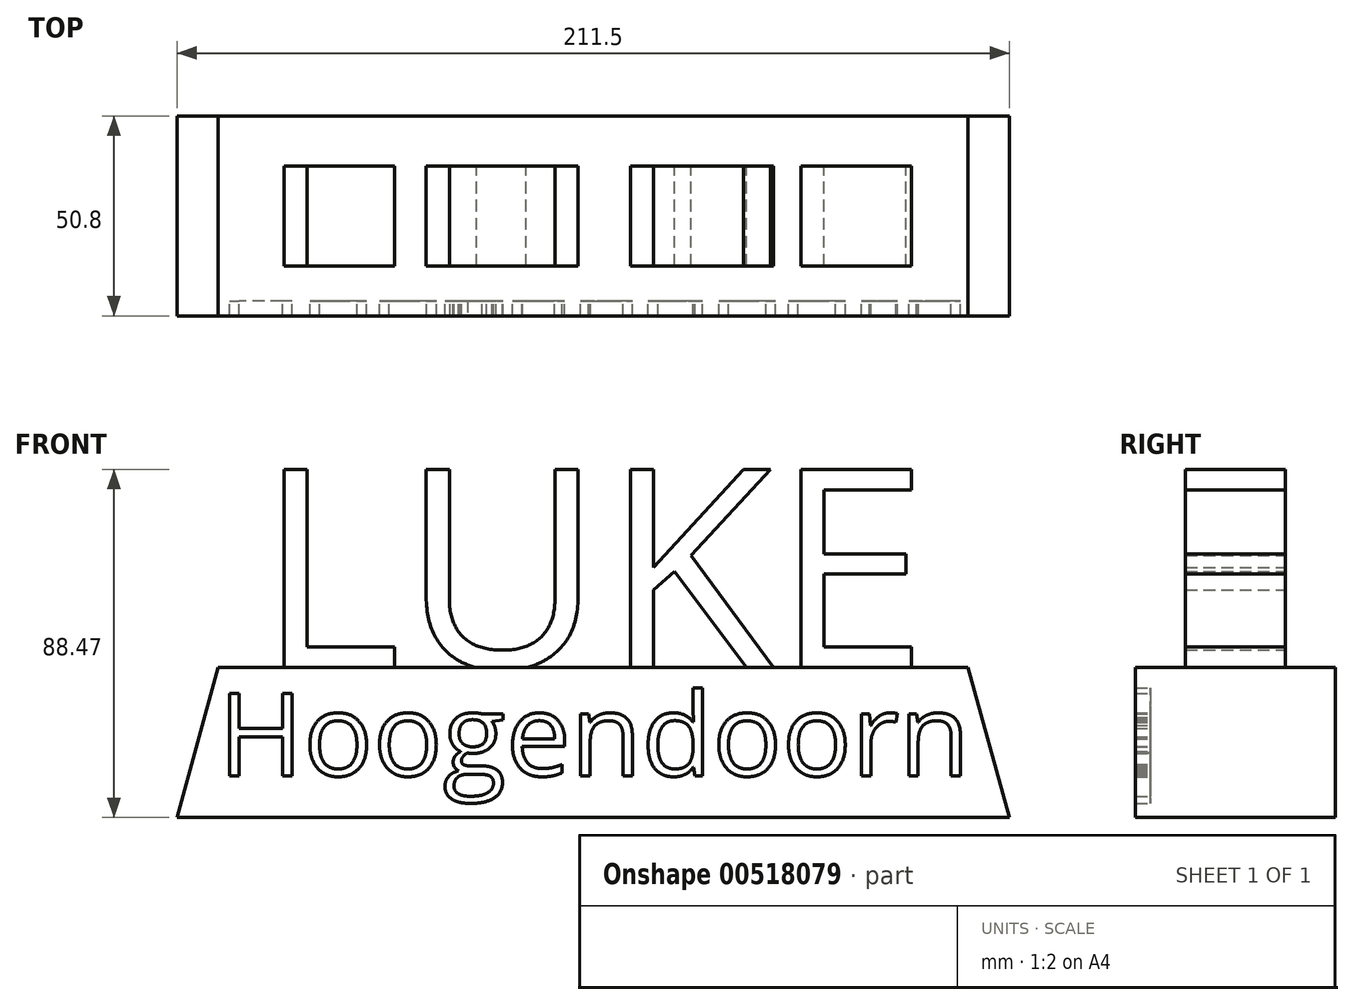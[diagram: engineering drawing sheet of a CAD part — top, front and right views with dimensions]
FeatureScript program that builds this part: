
annotation { "Feature Type Name" : "Feature", "Feature Type Description" : "" }
export const myFeature = defineFeature(function(context is Context, id is Id, definition is map)
    precondition{}
    {
        {
            var Q0;
            Q0=qCreatedBy(makeId("Front.planeOp"),FACE);
            var sketch = newSketch(context, id + "F0", { "sketchPlane" : qUnion([Q0])});
            skText(sketch, "E0", { "text": "LUKE\n", "fontName": "OpenSans-Regular.ttf"});
            skLineSegment(sketch, "E1.bottom", {"start": v(95.25, 0) * mm, "end": v(-95.25, 0) * mm});
            skLineSegment(sketch, "E1.top", {"start": v(95.25, -38.1) * mm, "end": v(-95.25, -38.1) * mm});
            skLineSegment(sketch, "E1.left", {"start": v(95.25, -6.35) * mm, "end": v(95.25, -27.46) * mm});
            skLineSegment(sketch, "E1.right", {"start": v(-95.25, -6.35) * mm, "end": v(-95.25, -27.46) * mm});
            skPoint(sketch, "E1.middle", {"position": v(0, -19.05) * mm});
            skLineSegment(sketch, "E2", {"start": v(-95.25, -6.35) * mm, "end": v(95.25, -6.35) * mm});
            skLineSegment(sketch, "E3.MirrorCS", {"start": v(-95.25, -27.46) * mm, "end": v(95.25, -27.46) * mm});
            skPoint(sketch, "E4.orphan", {"position": v(-95.25, -19.05) * mm});
            skPoint(sketch, "E5.end.orphan", {"position": v(95.25, -19.05) * mm});
            skText(sketch, "E6", { "text": "Hoogendoorn\n", "fontName": "OpenSans-Regular.ttf"});
            skLineSegment(sketch, "E7", {"start": v(-95.25, 0) * mm, "end": v(-105.75, -38.1) * mm});
            skLineSegment(sketch, "E8", {"start": v(-105.75, -38.1) * mm, "end": v(-95.25, -38.1) * mm});
            skLineSegment(sketch, "E9.MirrorCS", {"start": v(105.75, -38.1) * mm, "end": v(95.25, -38.1) * mm});
            skLineSegment(sketch, "E10.MirrorCS", {"start": v(95.25, 0) * mm, "end": v(105.75, -38.1) * mm});
            const initialGuessF0  = {"E0": [-0.08543, 0, 1, 0, 0.0508], "E6": [-0.09525, -0.02746, 1, 0, 0.02111]};
            skSetInitialGuess(sketch, initialGuessF0);
            skSolve(sketch);
        }
        {
            var Q0;
            Q0 = qSketchRegion(id + "F0", true);
            var Q1;
            Q1=makeQuery(id+"F0.imprint","IMPRINT",FACE,{"disambiguationData":[TD([[makeQuery(id+"F0.imprint","IMPRINT",EDGE,{"derivedFrom":sQuery(id+"F0.wireOp",EDGE,"E6.sketch_text.stroke-0")}),-1.0]])]});
            var Q2;
            {var subQ0=sQuery(id+"F0.wireOp",EDGE,"E6.sketch_text.stroke-1");Q2=makeQuery(id+"F0.imprint","IMPRINT",FACE,{"disambiguationData":[TD([[makeQuery(id+"F0.imprint","IMPRINT",EDGE,{"derivedFrom":subQ0}),1.0]])]});}
            var Q3;
            {var subQ29=sQuery(id+"F0.wireOp",EDGE,"E1.right");Q3=makeQuery(id+"F0.imprint","IMPRINT",FACE,{"disambiguationData":[TD([[makeQuery(id+"F0.imprint","IMPRINT",EDGE,{"derivedFrom":subQ29}),1.0]])]});}
            var Q4;
            {var subQ6=sQuery(id+"F0.wireOp",EDGE,"E6.sketch_text.stroke-29");Q4=makeQuery(id+"F0.imprint","IMPRINT",FACE,{"disambiguationData":[TD([[makeQuery(id+"F0.imprint","IMPRINT",EDGE,{"derivedFrom":subQ6}),-1.0]])]});}
            var Q5;
            {var subQ0=sQuery(id+"F0.wireOp",EDGE,"E6.sketch_text.stroke-31");var subQ1=sQuery(id+"F0.wireOp",EDGE,"E3.MirrorCS");var subQ2=makeQuery(id+"F0.imprint","INTERSECT",VERTEX,{"derivedFrom":[subQ1,subQ0]});Q5=makeQuery(id+"F0.imprint","IMPRINT",FACE,{"disambiguationData":[TD([[makeQuery(id+"F0.imprint","IMPRINT",EDGE,{"disambiguationData":[TD([[subQ2,-1.0]])],"derivedFrom":subQ1}),-1.0]])]});}
            var Q6;
            Q6=makeQuery(id+"F0.imprint","IMPRINT",FACE,{"disambiguationData":[TD([[makeQuery(id+"F0.imprint","IMPRINT",EDGE,{"derivedFrom":sQuery(id+"F0.wireOp",EDGE,"E6.sketch_text.stroke-38")}),1.0]])]});
            var Q7;
            Q7=makeQuery(id+"F0.imprint","IMPRINT",FACE,{"disambiguationData":[TD([[makeQuery(id+"F0.imprint","IMPRINT",EDGE,{"derivedFrom":sQuery(id+"F0.wireOp",EDGE,"E6.sketch_text.stroke-21")}),1.0]])]});
            var Q8;
            {var subQ6=sQuery(id+"F0.wireOp",EDGE,"E6.sketch_text.stroke-12");Q8=makeQuery(id+"F0.imprint","IMPRINT",FACE,{"disambiguationData":[TD([[makeQuery(id+"F0.imprint","IMPRINT",EDGE,{"derivedFrom":subQ6}),-1.0]])]});}
            var Q9;
            {var subQ0=sQuery(id+"F0.wireOp",EDGE,"E6.sketch_text.stroke-14");var subQ1=sQuery(id+"F0.wireOp",EDGE,"E3.MirrorCS");var subQ2=makeQuery(id+"F0.imprint","INTERSECT",VERTEX,{"derivedFrom":[subQ1,subQ0]});Q9=makeQuery(id+"F0.imprint","IMPRINT",FACE,{"disambiguationData":[TD([[makeQuery(id+"F0.imprint","IMPRINT",EDGE,{"disambiguationData":[TD([[subQ2,-1.0]])],"derivedFrom":subQ1}),-1.0]])]});}
            var Q10;
            Q10=makeQuery(id+"F0.imprint","IMPRINT",FACE,{"disambiguationData":[TD([[makeQuery(id+"F0.imprint","IMPRINT",EDGE,{"derivedFrom":sQuery(id+"F0.wireOp",EDGE,"E6.sketch_text.stroke-84")}),1.0]])]});
            var Q11;
            Q11=makeQuery(id+"F0.imprint","IMPRINT",FACE,{"disambiguationData":[TD([[makeQuery(id+"F0.imprint","IMPRINT",EDGE,{"derivedFrom":sQuery(id+"F0.wireOp",EDGE,"E6.sketch_text.stroke-46")}),-1.0]])]});
            var Q12;
            {var subQ5=sQuery(id+"F0.wireOp",EDGE,"E6.sketch_text.stroke-81");Q12=makeQuery(id+"F0.imprint","IMPRINT",FACE,{"disambiguationData":[TD([[makeQuery(id+"F0.imprint","IMPRINT",EDGE,{"derivedFrom":subQ5}),1.0]])]});}
            var Q13;
            Q13=makeQuery(id+"F0.imprint","IMPRINT",FACE,{"disambiguationData":[TD([[makeQuery(id+"F0.imprint","IMPRINT",EDGE,{"derivedFrom":sQuery(id+"F0.wireOp",EDGE,"E6.sketch_text.stroke-75")}),1.0]])]});
            var Q14;
            {var subQ11=sQuery(id+"F0.wireOp",EDGE,"E6.sketch_text.stroke-59");Q14=makeQuery(id+"F0.imprint","IMPRINT",FACE,{"disambiguationData":[TD([[makeQuery(id+"F0.imprint","IMPRINT",EDGE,{"derivedFrom":subQ11}),-1.0]])]});}
            var Q15;
            Q15=makeQuery(id+"F0.imprint","IMPRINT",FACE,{"disambiguationData":[TD([[makeQuery(id+"F0.imprint","IMPRINT",EDGE,{"derivedFrom":sQuery(id+"F0.wireOp",EDGE,"E6.sketch_text.stroke-104")}),1.0]])]});
            var Q16;
            {var subQ5=sQuery(id+"F0.wireOp",EDGE,"E6.sketch_text.stroke-91");Q16=makeQuery(id+"F0.imprint","IMPRINT",FACE,{"disambiguationData":[TD([[makeQuery(id+"F0.imprint","IMPRINT",EDGE,{"derivedFrom":subQ5}),-1.0]])]});}
            var Q17;
            {var subQ5=sQuery(id+"F0.wireOp",EDGE,"E6.sketch_text.stroke-103");Q17=makeQuery(id+"F0.imprint","IMPRINT",FACE,{"disambiguationData":[TD([[makeQuery(id+"F0.imprint","IMPRINT",EDGE,{"derivedFrom":subQ5}),-1.0]])]});}
            var Q18;
            {var subQ0=sQuery(id+"F0.wireOp",EDGE,"E6.sketch_text.stroke-109");Q18=makeQuery(id+"F0.imprint","IMPRINT",FACE,{"disambiguationData":[TD([[makeQuery(id+"F0.imprint","IMPRINT",EDGE,{"derivedFrom":subQ0}),1.0]])]});}
            var Q19;
            Q19=makeQuery(id+"F0.imprint","IMPRINT",FACE,{"disambiguationData":[TD([[makeQuery(id+"F0.imprint","IMPRINT",EDGE,{"derivedFrom":sQuery(id+"F0.wireOp",EDGE,"E6.sketch_text.stroke-109")}),-1.0]])]});
            var Q20;
            {var subQ9=sQuery(id+"F0.wireOp",EDGE,"E6.sketch_text.stroke-126");Q20=makeQuery(id+"F0.imprint","IMPRINT",FACE,{"disambiguationData":[TD([[makeQuery(id+"F0.imprint","IMPRINT",EDGE,{"derivedFrom":subQ9}),-1.0]])]});}
            var Q21;
            Q21=makeQuery(id+"F0.imprint","IMPRINT",FACE,{"disambiguationData":[TD([[makeQuery(id+"F0.imprint","IMPRINT",EDGE,{"derivedFrom":sQuery(id+"F0.wireOp",EDGE,"E6.sketch_text.stroke-141")}),1.0]])]});
            var Q22;
            {var subQ4=sQuery(id+"F0.wireOp",EDGE,"E6.sketch_text.stroke-126");Q22=makeQuery(id+"F0.imprint","IMPRINT",FACE,{"disambiguationData":[TD([[makeQuery(id+"F0.imprint","IMPRINT",EDGE,{"derivedFrom":subQ4}),1.0]])]});}
            var Q23;
            {var subQ5=sQuery(id+"F0.wireOp",EDGE,"E6.sketch_text.stroke-137");Q23=makeQuery(id+"F0.imprint","IMPRINT",FACE,{"disambiguationData":[TD([[makeQuery(id+"F0.imprint","IMPRINT",EDGE,{"derivedFrom":subQ5}),-1.0]])]});}
            var Q24;
            {var subQ0=sQuery(id+"F0.wireOp",EDGE,"E6.sketch_text.stroke-128");var subQ1=sQuery(id+"F0.wireOp",EDGE,"E3.MirrorCS");var subQ2=makeQuery(id+"F0.imprint","INTERSECT",VERTEX,{"derivedFrom":[subQ1,subQ0]});Q24=makeQuery(id+"F0.imprint","IMPRINT",FACE,{"disambiguationData":[TD([[makeQuery(id+"F0.imprint","IMPRINT",EDGE,{"disambiguationData":[TD([[subQ2,-1.0]])],"derivedFrom":subQ1}),-1.0]])]});}
            var Q25;
            Q25=makeQuery(id+"F0.imprint","IMPRINT",FACE,{"disambiguationData":[TD([[makeQuery(id+"F0.imprint","IMPRINT",EDGE,{"derivedFrom":sQuery(id+"F0.wireOp",EDGE,"E6.sketch_text.stroke-159")}),1.0]])]});
            var Q26;
            {var subQ6=sQuery(id+"F0.wireOp",EDGE,"E6.sketch_text.stroke-150");Q26=makeQuery(id+"F0.imprint","IMPRINT",FACE,{"disambiguationData":[TD([[makeQuery(id+"F0.imprint","IMPRINT",EDGE,{"derivedFrom":subQ6}),-1.0]])]});}
            var Q27;
            {var subQ3=sQuery(id+"F0.wireOp",EDGE,"E1.left");Q27=makeQuery(id+"F0.imprint","IMPRINT",FACE,{"disambiguationData":[TD([[makeQuery(id+"F0.imprint","IMPRINT",EDGE,{"derivedFrom":subQ3}),-1.0]])]});}
            var Q28;
            Q28=makeQuery(id+"F0.imprint","IMPRINT",FACE,{"disambiguationData":[TD([[makeQuery(id+"F0.imprint","IMPRINT",EDGE,{"derivedFrom":sQuery(id+"F0.wireOp",EDGE,"E6.sketch_text.stroke-176")}),1.0]])]});
            var Q29;
            {var subQ6=sQuery(id+"F0.wireOp",EDGE,"E6.sketch_text.stroke-167");Q29=makeQuery(id+"F0.imprint","IMPRINT",FACE,{"disambiguationData":[TD([[makeQuery(id+"F0.imprint","IMPRINT",EDGE,{"derivedFrom":subQ6}),-1.0]])]});}
            var Q30;
            {var subQ0=sQuery(id+"F0.wireOp",EDGE,"E6.sketch_text.stroke-169");var subQ1=sQuery(id+"F0.wireOp",EDGE,"E3.MirrorCS");var subQ2=makeQuery(id+"F0.imprint","INTERSECT",VERTEX,{"derivedFrom":[subQ1,subQ0]});Q30=makeQuery(id+"F0.imprint","IMPRINT",FACE,{"disambiguationData":[TD([[makeQuery(id+"F0.imprint","IMPRINT",EDGE,{"disambiguationData":[TD([[subQ2,-1.0]])],"derivedFrom":subQ1}),-1.0]])]});}
            var Q31;
            {var subQ0=sQuery(id+"F0.wireOp",EDGE,"E6.sketch_text.stroke-152");var subQ1=sQuery(id+"F0.wireOp",EDGE,"E3.MirrorCS");var subQ2=makeQuery(id+"F0.imprint","INTERSECT",VERTEX,{"derivedFrom":[subQ1,subQ0]});Q31=makeQuery(id+"F0.imprint","IMPRINT",FACE,{"disambiguationData":[TD([[makeQuery(id+"F0.imprint","IMPRINT",EDGE,{"disambiguationData":[TD([[subQ2,-1.0]])],"derivedFrom":subQ1}),-1.0]])]});}
            var Q32;
            Q32=makeQuery(id+"F0.imprint","IMPRINT",FACE,{"disambiguationData":[TD([[makeQuery(id+"F0.imprint","IMPRINT",EDGE,{"derivedFrom":sQuery(id+"F0.wireOp",EDGE,"E6.sketch_text.stroke-184")}),-1.0]])]});
            var Q33;
            {var subQ0=sQuery(id+"F0.wireOp",EDGE,"E6.sketch_text.stroke-197");Q33=makeQuery(id+"F0.imprint","IMPRINT",FACE,{"disambiguationData":[TD([[makeQuery(id+"F0.imprint","IMPRINT",EDGE,{"derivedFrom":subQ0}),1.0]])]});}
            var Q34;
            Q34=makeQuery(id+"F0.imprint","IMPRINT",FACE,{"disambiguationData":[TD([[makeQuery(id+"F0.imprint","IMPRINT",EDGE,{"derivedFrom":sQuery(id+"F0.wireOp",EDGE,"E6.sketch_text.stroke-197")}),-1.0]])]});
            extrude(context, id + "F1", {"entities" : qUnion([Q0, Q1, Q2, Q3, Q4, Q5, Q6, Q7, Q8, Q9, Q10, Q11, Q12, Q13, Q14, Q15, Q16, Q17, Q18, Q19, Q20, Q21, Q22, Q23, Q24, Q25, Q26, Q27, Q28, Q29, Q30, Q31, Q32, Q33, Q34]), "depth" : 25.4 * mm, "offsetDistance" : 25.4 * mm});
        }
        {
            var Q0;
            {var subQ6=sQuery(id+"F0.wireOp",EDGE,"E6.sketch_text.stroke-12");Q0=makeQuery(id+"F0.imprint","IMPRINT",FACE,{"disambiguationData":[TD([[makeQuery(id+"F0.imprint","IMPRINT",EDGE,{"derivedFrom":subQ6}),-1.0]])]});}
            var Q1;
            Q1=makeQuery(id+"F0.imprint","IMPRINT",FACE,{"disambiguationData":[TD([[makeQuery(id+"F0.imprint","IMPRINT",EDGE,{"derivedFrom":sQuery(id+"F0.wireOp",EDGE,"E6.sketch_text.stroke-0")}),-1.0]])]});
            var Q2;
            {var subQ0=sQuery(id+"F0.wireOp",EDGE,"E6.sketch_text.stroke-14");var subQ1=sQuery(id+"F0.wireOp",EDGE,"E3.MirrorCS");var subQ2=makeQuery(id+"F0.imprint","INTERSECT",VERTEX,{"derivedFrom":[subQ1,subQ0]});Q2=makeQuery(id+"F0.imprint","IMPRINT",FACE,{"disambiguationData":[TD([[makeQuery(id+"F0.imprint","IMPRINT",EDGE,{"disambiguationData":[TD([[subQ2,-1.0]])],"derivedFrom":subQ1}),-1.0]])]});}
            var Q3;
            {var subQ6=sQuery(id+"F0.wireOp",EDGE,"E6.sketch_text.stroke-29");Q3=makeQuery(id+"F0.imprint","IMPRINT",FACE,{"disambiguationData":[TD([[makeQuery(id+"F0.imprint","IMPRINT",EDGE,{"derivedFrom":subQ6}),-1.0]])]});}
            var Q4;
            {var subQ0=sQuery(id+"F0.wireOp",EDGE,"E6.sketch_text.stroke-31");var subQ1=sQuery(id+"F0.wireOp",EDGE,"E3.MirrorCS");var subQ2=makeQuery(id+"F0.imprint","INTERSECT",VERTEX,{"derivedFrom":[subQ1,subQ0]});Q4=makeQuery(id+"F0.imprint","IMPRINT",FACE,{"disambiguationData":[TD([[makeQuery(id+"F0.imprint","IMPRINT",EDGE,{"disambiguationData":[TD([[subQ2,-1.0]])],"derivedFrom":subQ1}),-1.0]])]});}
            var Q5;
            {var subQ11=sQuery(id+"F0.wireOp",EDGE,"E6.sketch_text.stroke-59");Q5=makeQuery(id+"F0.imprint","IMPRINT",FACE,{"disambiguationData":[TD([[makeQuery(id+"F0.imprint","IMPRINT",EDGE,{"derivedFrom":subQ11}),-1.0]])]});}
            var Q6;
            Q6=makeQuery(id+"F0.imprint","IMPRINT",FACE,{"disambiguationData":[TD([[makeQuery(id+"F0.imprint","IMPRINT",EDGE,{"derivedFrom":sQuery(id+"F0.wireOp",EDGE,"E6.sketch_text.stroke-46")}),-1.0]])]});
            var Q7;
            {var subQ5=sQuery(id+"F0.wireOp",EDGE,"E6.sketch_text.stroke-91");Q7=makeQuery(id+"F0.imprint","IMPRINT",FACE,{"disambiguationData":[TD([[makeQuery(id+"F0.imprint","IMPRINT",EDGE,{"derivedFrom":subQ5}),-1.0]])]});}
            var Q8;
            Q8=makeQuery(id+"F0.imprint","IMPRINT",FACE,{"disambiguationData":[TD([[makeQuery(id+"F0.imprint","IMPRINT",EDGE,{"derivedFrom":sQuery(id+"F0.wireOp",EDGE,"E6.sketch_text.stroke-109")}),-1.0]])]});
            var Q9;
            {var subQ9=sQuery(id+"F0.wireOp",EDGE,"E6.sketch_text.stroke-126");Q9=makeQuery(id+"F0.imprint","IMPRINT",FACE,{"disambiguationData":[TD([[makeQuery(id+"F0.imprint","IMPRINT",EDGE,{"derivedFrom":subQ9}),-1.0]])]});}
            var Q10;
            {var subQ5=sQuery(id+"F0.wireOp",EDGE,"E6.sketch_text.stroke-137");Q10=makeQuery(id+"F0.imprint","IMPRINT",FACE,{"disambiguationData":[TD([[makeQuery(id+"F0.imprint","IMPRINT",EDGE,{"derivedFrom":subQ5}),-1.0]])]});}
            var Q11;
            {var subQ0=sQuery(id+"F0.wireOp",EDGE,"E6.sketch_text.stroke-128");var subQ1=sQuery(id+"F0.wireOp",EDGE,"E3.MirrorCS");var subQ2=makeQuery(id+"F0.imprint","INTERSECT",VERTEX,{"derivedFrom":[subQ1,subQ0]});Q11=makeQuery(id+"F0.imprint","IMPRINT",FACE,{"disambiguationData":[TD([[makeQuery(id+"F0.imprint","IMPRINT",EDGE,{"disambiguationData":[TD([[subQ2,-1.0]])],"derivedFrom":subQ1}),-1.0]])]});}
            var Q12;
            {var subQ5=sQuery(id+"F0.wireOp",EDGE,"E6.sketch_text.stroke-103");Q12=makeQuery(id+"F0.imprint","IMPRINT",FACE,{"disambiguationData":[TD([[makeQuery(id+"F0.imprint","IMPRINT",EDGE,{"derivedFrom":subQ5}),-1.0]])]});}
            var Q13;
            {var subQ6=sQuery(id+"F0.wireOp",EDGE,"E6.sketch_text.stroke-150");Q13=makeQuery(id+"F0.imprint","IMPRINT",FACE,{"disambiguationData":[TD([[makeQuery(id+"F0.imprint","IMPRINT",EDGE,{"derivedFrom":subQ6}),-1.0]])]});}
            var Q14;
            {var subQ0=sQuery(id+"F0.wireOp",EDGE,"E6.sketch_text.stroke-152");var subQ1=sQuery(id+"F0.wireOp",EDGE,"E3.MirrorCS");var subQ2=makeQuery(id+"F0.imprint","INTERSECT",VERTEX,{"derivedFrom":[subQ1,subQ0]});Q14=makeQuery(id+"F0.imprint","IMPRINT",FACE,{"disambiguationData":[TD([[makeQuery(id+"F0.imprint","IMPRINT",EDGE,{"disambiguationData":[TD([[subQ2,-1.0]])],"derivedFrom":subQ1}),-1.0]])]});}
            var Q15;
            {var subQ6=sQuery(id+"F0.wireOp",EDGE,"E6.sketch_text.stroke-167");Q15=makeQuery(id+"F0.imprint","IMPRINT",FACE,{"disambiguationData":[TD([[makeQuery(id+"F0.imprint","IMPRINT",EDGE,{"derivedFrom":subQ6}),-1.0]])]});}
            var Q16;
            {var subQ0=sQuery(id+"F0.wireOp",EDGE,"E6.sketch_text.stroke-169");var subQ1=sQuery(id+"F0.wireOp",EDGE,"E3.MirrorCS");var subQ2=makeQuery(id+"F0.imprint","INTERSECT",VERTEX,{"derivedFrom":[subQ1,subQ0]});Q16=makeQuery(id+"F0.imprint","IMPRINT",FACE,{"disambiguationData":[TD([[makeQuery(id+"F0.imprint","IMPRINT",EDGE,{"disambiguationData":[TD([[subQ2,-1.0]])],"derivedFrom":subQ1}),-1.0]])]});}
            var Q17;
            Q17=makeQuery(id+"F0.imprint","IMPRINT",FACE,{"disambiguationData":[TD([[makeQuery(id+"F0.imprint","IMPRINT",EDGE,{"derivedFrom":sQuery(id+"F0.wireOp",EDGE,"E6.sketch_text.stroke-184")}),-1.0]])]});
            var Q18;
            Q18=makeQuery(id+"F0.imprint","IMPRINT",FACE,{"disambiguationData":[TD([[makeQuery(id+"F0.imprint","IMPRINT",EDGE,{"derivedFrom":sQuery(id+"F0.wireOp",EDGE,"E6.sketch_text.stroke-197")}),-1.0]])]});
            extrude(context, id + "F2", {"entities" : qUnion([Q0, Q1, Q2, Q3, Q4, Q5, Q6, Q7, Q8, Q9, Q10, Q11, Q12, Q13, Q14, Q15, Q16, Q17, Q18]), "operationType" : NewBodyOperationType.REMOVE, "depth" : 25.4 * mm, "offsetDistance" : 25.4 * mm, "hasSecondDirection" : true, "secondDirectionOppositeDirection" : false, "secondDirectionDepth" : 21.59 * mm});
        }
        {
            var Q0;
            {var subQ0=sQuery(id+"F0.wireOp",EDGE,"E10.MirrorCS");var subQ1=sQuery(id+"F0.wireOp",EDGE,"E7");var subQ2=sQuery(id+"F0.wireOp",EDGE,"E9.MirrorCS");var subQ3=sQuery(id+"F0.wireOp",EDGE,"E8");var subQ4=sQuery(id+"F0.wireOp",EDGE,"E1.top");var subQ5=sQuery(id+"F0.wireOp",EDGE,"E1.bottom");var subQ6=sQuery(id+"F0.wireOp",EDGE,"E0.sketch_text.stroke-0");var subQ7=sQuery(id+"F0.wireOp",EDGE,"E0.sketch_text.stroke-21");var subQ8=sQuery(id+"F0.wireOp",EDGE,"E0.sketch_text.stroke-23");var subQ9=sQuery(id+"F0.wireOp",EDGE,"E0.sketch_text.stroke-36");var subQ10=sQuery(id+"F0.wireOp",EDGE,"E0.sketch_text.stroke-35");var subQ11=sQuery(id+"F0.wireOp",EDGE,"E0.sketch_text.stroke-34");var subQ12=sQuery(id+"F0.wireOp",EDGE,"E0.sketch_text.stroke-33");var subQ13=sQuery(id+"F0.wireOp",EDGE,"E0.sketch_text.stroke-31");var subQ14=sQuery(id+"F0.wireOp",EDGE,"E0.sketch_text.stroke-30");var subQ15=sQuery(id+"F0.wireOp",EDGE,"E0.sketch_text.stroke-29");var subQ16=sQuery(id+"F0.wireOp",EDGE,"E0.sketch_text.stroke-28");var subQ17=sQuery(id+"F0.wireOp",EDGE,"E0.sketch_text.stroke-27");var subQ18=sQuery(id+"F0.wireOp",EDGE,"E0.sketch_text.stroke-26");var subQ19=sQuery(id+"F0.wireOp",EDGE,"E0.sketch_text.stroke-25");var subQ20=sQuery(id+"F0.wireOp",EDGE,"E0.sketch_text.stroke-22");var subQ21=sQuery(id+"F0.wireOp",EDGE,"E0.sketch_text.stroke-17");var subQ22=sQuery(id+"F0.wireOp",EDGE,"E0.sketch_text.stroke-16");var subQ23=sQuery(id+"F0.wireOp",EDGE,"E0.sketch_text.stroke-15");var subQ24=sQuery(id+"F0.wireOp",EDGE,"E0.sketch_text.stroke-14");var subQ25=sQuery(id+"F0.wireOp",EDGE,"E0.sketch_text.stroke-13");var subQ26=sQuery(id+"F0.wireOp",EDGE,"E0.sketch_text.stroke-12");var subQ27=sQuery(id+"F0.wireOp",EDGE,"E0.sketch_text.stroke-11");var subQ28=sQuery(id+"F0.wireOp",EDGE,"E0.sketch_text.stroke-10");var subQ29=sQuery(id+"F0.wireOp",EDGE,"E0.sketch_text.stroke-9");var subQ30=sQuery(id+"F0.wireOp",EDGE,"E0.sketch_text.stroke-8");var subQ31=sQuery(id+"F0.wireOp",EDGE,"E0.sketch_text.stroke-7");var subQ32=sQuery(id+"F0.wireOp",EDGE,"E0.sketch_text.stroke-6");var subQ33=sQuery(id+"F0.wireOp",EDGE,"E0.sketch_text.stroke-4");var subQ34=sQuery(id+"F0.wireOp",EDGE,"E0.sketch_text.stroke-3");var subQ35=sQuery(id+"F0.wireOp",EDGE,"E0.sketch_text.stroke-2");var subQ36=sQuery(id+"F0.wireOp",EDGE,"E0.sketch_text.stroke-1");var subQ37=sQuery(id+"F0.wireOp",EDGE,"E0.sketch_text.stroke-43");var subQ38=sQuery(id+"F0.wireOp",EDGE,"E0.sketch_text.stroke-42");var subQ39=sQuery(id+"F0.wireOp",EDGE,"E0.sketch_text.stroke-41");var subQ40=sQuery(id+"F0.wireOp",EDGE,"E0.sketch_text.stroke-40");var subQ41=sQuery(id+"F0.wireOp",EDGE,"E0.sketch_text.stroke-39");var subQ42=sQuery(id+"F0.wireOp",EDGE,"E0.sketch_text.stroke-38");var subQ43=sQuery(id+"F0.wireOp",EDGE,"E0.sketch_text.stroke-37");var subQ44=sQuery(id+"F0.wireOp",EDGE,"E0.sketch_text.stroke-18");var subQ45=sQuery(id+"F0.wireOp",EDGE,"E0.sketch_text.stroke-19");Q0=makeQuery(id+"F2.boolean.opBoolean","SPLIT",FACE,{"disambiguationData":[TD([makeQuery(id+"F1.opExtrude","SWEPT_FACE",FACE,{"disambiguationData":[OSD([subQ6])]})])],"derivedFrom":makeQuery(id+"F1.opExtrude","CAP_FACE",FACE,{"disambiguationData":[OSD([subQ6,subQ36,subQ35,subQ34,subQ33,subQ32,subQ31,subQ30,subQ29,subQ28,subQ27,subQ26,subQ25,subQ24,subQ23,subQ22,subQ21,subQ44,subQ45,subQ7,subQ20,subQ8,subQ19,subQ18,subQ17,subQ16,subQ15,subQ14,subQ13,subQ12,subQ11,subQ10,subQ9,subQ43,subQ42,subQ41,subQ40,subQ39,subQ38,subQ37,subQ5,subQ4,subQ1,subQ3,subQ2,subQ0])],"isStart":false})});}
            var Q1;
            Q1=makeQuery(id+"F2.boolean.opBoolean","SPLIT",FACE,{"disambiguationData":[TD([makeQuery(id+"F2.opExtrude","SWEPT_FACE",FACE,{"disambiguationData":[OSD([sQuery(id+"F0.wireOp",EDGE,"E6.sketch_text.stroke-21")])]})])],"derivedFrom":makeQuery(id+"F1.opExtrude","CAP_FACE",FACE,{"disambiguationData":[OSD([sQuery(id+"F0.wireOp",EDGE,"E0.sketch_text.stroke-0"),sQuery(id+"F0.wireOp",EDGE,"E0.sketch_text.stroke-1"),sQuery(id+"F0.wireOp",EDGE,"E0.sketch_text.stroke-2"),sQuery(id+"F0.wireOp",EDGE,"E0.sketch_text.stroke-3"),sQuery(id+"F0.wireOp",EDGE,"E0.sketch_text.stroke-4"),sQuery(id+"F0.wireOp",EDGE,"E0.sketch_text.stroke-6"),sQuery(id+"F0.wireOp",EDGE,"E0.sketch_text.stroke-7"),sQuery(id+"F0.wireOp",EDGE,"E0.sketch_text.stroke-8"),sQuery(id+"F0.wireOp",EDGE,"E0.sketch_text.stroke-9"),sQuery(id+"F0.wireOp",EDGE,"E0.sketch_text.stroke-10"),sQuery(id+"F0.wireOp",EDGE,"E0.sketch_text.stroke-11"),sQuery(id+"F0.wireOp",EDGE,"E0.sketch_text.stroke-12"),sQuery(id+"F0.wireOp",EDGE,"E0.sketch_text.stroke-13"),sQuery(id+"F0.wireOp",EDGE,"E0.sketch_text.stroke-14"),sQuery(id+"F0.wireOp",EDGE,"E0.sketch_text.stroke-15"),sQuery(id+"F0.wireOp",EDGE,"E0.sketch_text.stroke-16"),sQuery(id+"F0.wireOp",EDGE,"E0.sketch_text.stroke-17"),sQuery(id+"F0.wireOp",EDGE,"E0.sketch_text.stroke-18"),sQuery(id+"F0.wireOp",EDGE,"E0.sketch_text.stroke-19"),sQuery(id+"F0.wireOp",EDGE,"E0.sketch_text.stroke-21"),sQuery(id+"F0.wireOp",EDGE,"E0.sketch_text.stroke-22"),sQuery(id+"F0.wireOp",EDGE,"E0.sketch_text.stroke-23"),sQuery(id+"F0.wireOp",EDGE,"E0.sketch_text.stroke-25"),sQuery(id+"F0.wireOp",EDGE,"E0.sketch_text.stroke-26"),sQuery(id+"F0.wireOp",EDGE,"E0.sketch_text.stroke-27"),sQuery(id+"F0.wireOp",EDGE,"E0.sketch_text.stroke-28"),sQuery(id+"F0.wireOp",EDGE,"E0.sketch_text.stroke-29"),sQuery(id+"F0.wireOp",EDGE,"E0.sketch_text.stroke-30"),sQuery(id+"F0.wireOp",EDGE,"E0.sketch_text.stroke-31"),sQuery(id+"F0.wireOp",EDGE,"E0.sketch_text.stroke-33"),sQuery(id+"F0.wireOp",EDGE,"E0.sketch_text.stroke-34"),sQuery(id+"F0.wireOp",EDGE,"E0.sketch_text.stroke-35"),sQuery(id+"F0.wireOp",EDGE,"E0.sketch_text.stroke-36"),sQuery(id+"F0.wireOp",EDGE,"E0.sketch_text.stroke-37"),sQuery(id+"F0.wireOp",EDGE,"E0.sketch_text.stroke-38"),sQuery(id+"F0.wireOp",EDGE,"E0.sketch_text.stroke-39"),sQuery(id+"F0.wireOp",EDGE,"E0.sketch_text.stroke-40"),sQuery(id+"F0.wireOp",EDGE,"E0.sketch_text.stroke-41"),sQuery(id+"F0.wireOp",EDGE,"E0.sketch_text.stroke-42"),sQuery(id+"F0.wireOp",EDGE,"E0.sketch_text.stroke-43"),sQuery(id+"F0.wireOp",EDGE,"E1.bottom"),sQuery(id+"F0.wireOp",EDGE,"E1.top"),sQuery(id+"F0.wireOp",EDGE,"E7"),sQuery(id+"F0.wireOp",EDGE,"E8"),sQuery(id+"F0.wireOp",EDGE,"E9.MirrorCS"),sQuery(id+"F0.wireOp",EDGE,"E10.MirrorCS")])],"isStart":false})});
            var Q2;
            Q2=makeQuery(id+"F2.boolean.opBoolean","SPLIT",FACE,{"disambiguationData":[TD([makeQuery(id+"F2.opExtrude","SWEPT_FACE",FACE,{"disambiguationData":[OSD([sQuery(id+"F0.wireOp",EDGE,"E6.sketch_text.stroke-38")])]})])],"derivedFrom":makeQuery(id+"F1.opExtrude","CAP_FACE",FACE,{"disambiguationData":[OSD([sQuery(id+"F0.wireOp",EDGE,"E0.sketch_text.stroke-0"),sQuery(id+"F0.wireOp",EDGE,"E0.sketch_text.stroke-1"),sQuery(id+"F0.wireOp",EDGE,"E0.sketch_text.stroke-2"),sQuery(id+"F0.wireOp",EDGE,"E0.sketch_text.stroke-3"),sQuery(id+"F0.wireOp",EDGE,"E0.sketch_text.stroke-4"),sQuery(id+"F0.wireOp",EDGE,"E0.sketch_text.stroke-6"),sQuery(id+"F0.wireOp",EDGE,"E0.sketch_text.stroke-7"),sQuery(id+"F0.wireOp",EDGE,"E0.sketch_text.stroke-8"),sQuery(id+"F0.wireOp",EDGE,"E0.sketch_text.stroke-9"),sQuery(id+"F0.wireOp",EDGE,"E0.sketch_text.stroke-10"),sQuery(id+"F0.wireOp",EDGE,"E0.sketch_text.stroke-11"),sQuery(id+"F0.wireOp",EDGE,"E0.sketch_text.stroke-12"),sQuery(id+"F0.wireOp",EDGE,"E0.sketch_text.stroke-13"),sQuery(id+"F0.wireOp",EDGE,"E0.sketch_text.stroke-14"),sQuery(id+"F0.wireOp",EDGE,"E0.sketch_text.stroke-15"),sQuery(id+"F0.wireOp",EDGE,"E0.sketch_text.stroke-16"),sQuery(id+"F0.wireOp",EDGE,"E0.sketch_text.stroke-17"),sQuery(id+"F0.wireOp",EDGE,"E0.sketch_text.stroke-18"),sQuery(id+"F0.wireOp",EDGE,"E0.sketch_text.stroke-19"),sQuery(id+"F0.wireOp",EDGE,"E0.sketch_text.stroke-21"),sQuery(id+"F0.wireOp",EDGE,"E0.sketch_text.stroke-22"),sQuery(id+"F0.wireOp",EDGE,"E0.sketch_text.stroke-23"),sQuery(id+"F0.wireOp",EDGE,"E0.sketch_text.stroke-25"),sQuery(id+"F0.wireOp",EDGE,"E0.sketch_text.stroke-26"),sQuery(id+"F0.wireOp",EDGE,"E0.sketch_text.stroke-27"),sQuery(id+"F0.wireOp",EDGE,"E0.sketch_text.stroke-28"),sQuery(id+"F0.wireOp",EDGE,"E0.sketch_text.stroke-29"),sQuery(id+"F0.wireOp",EDGE,"E0.sketch_text.stroke-30"),sQuery(id+"F0.wireOp",EDGE,"E0.sketch_text.stroke-31"),sQuery(id+"F0.wireOp",EDGE,"E0.sketch_text.stroke-33"),sQuery(id+"F0.wireOp",EDGE,"E0.sketch_text.stroke-34"),sQuery(id+"F0.wireOp",EDGE,"E0.sketch_text.stroke-35"),sQuery(id+"F0.wireOp",EDGE,"E0.sketch_text.stroke-36"),sQuery(id+"F0.wireOp",EDGE,"E0.sketch_text.stroke-37"),sQuery(id+"F0.wireOp",EDGE,"E0.sketch_text.stroke-38"),sQuery(id+"F0.wireOp",EDGE,"E0.sketch_text.stroke-39"),sQuery(id+"F0.wireOp",EDGE,"E0.sketch_text.stroke-40"),sQuery(id+"F0.wireOp",EDGE,"E0.sketch_text.stroke-41"),sQuery(id+"F0.wireOp",EDGE,"E0.sketch_text.stroke-42"),sQuery(id+"F0.wireOp",EDGE,"E0.sketch_text.stroke-43"),sQuery(id+"F0.wireOp",EDGE,"E1.bottom"),sQuery(id+"F0.wireOp",EDGE,"E1.top"),sQuery(id+"F0.wireOp",EDGE,"E7"),sQuery(id+"F0.wireOp",EDGE,"E8"),sQuery(id+"F0.wireOp",EDGE,"E9.MirrorCS"),sQuery(id+"F0.wireOp",EDGE,"E10.MirrorCS")])],"isStart":false})});
            var Q3;
            Q3=makeQuery(id+"F2.boolean.opBoolean","SPLIT",FACE,{"disambiguationData":[TD([makeQuery(id+"F2.opExtrude","SWEPT_FACE",FACE,{"disambiguationData":[OSD([sQuery(id+"F0.wireOp",EDGE,"E6.sketch_text.stroke-84")])]})])],"derivedFrom":makeQuery(id+"F1.opExtrude","CAP_FACE",FACE,{"disambiguationData":[OSD([sQuery(id+"F0.wireOp",EDGE,"E0.sketch_text.stroke-0"),sQuery(id+"F0.wireOp",EDGE,"E0.sketch_text.stroke-1"),sQuery(id+"F0.wireOp",EDGE,"E0.sketch_text.stroke-2"),sQuery(id+"F0.wireOp",EDGE,"E0.sketch_text.stroke-3"),sQuery(id+"F0.wireOp",EDGE,"E0.sketch_text.stroke-4"),sQuery(id+"F0.wireOp",EDGE,"E0.sketch_text.stroke-6"),sQuery(id+"F0.wireOp",EDGE,"E0.sketch_text.stroke-7"),sQuery(id+"F0.wireOp",EDGE,"E0.sketch_text.stroke-8"),sQuery(id+"F0.wireOp",EDGE,"E0.sketch_text.stroke-9"),sQuery(id+"F0.wireOp",EDGE,"E0.sketch_text.stroke-10"),sQuery(id+"F0.wireOp",EDGE,"E0.sketch_text.stroke-11"),sQuery(id+"F0.wireOp",EDGE,"E0.sketch_text.stroke-12"),sQuery(id+"F0.wireOp",EDGE,"E0.sketch_text.stroke-13"),sQuery(id+"F0.wireOp",EDGE,"E0.sketch_text.stroke-14"),sQuery(id+"F0.wireOp",EDGE,"E0.sketch_text.stroke-15"),sQuery(id+"F0.wireOp",EDGE,"E0.sketch_text.stroke-16"),sQuery(id+"F0.wireOp",EDGE,"E0.sketch_text.stroke-17"),sQuery(id+"F0.wireOp",EDGE,"E0.sketch_text.stroke-18"),sQuery(id+"F0.wireOp",EDGE,"E0.sketch_text.stroke-19"),sQuery(id+"F0.wireOp",EDGE,"E0.sketch_text.stroke-21"),sQuery(id+"F0.wireOp",EDGE,"E0.sketch_text.stroke-22"),sQuery(id+"F0.wireOp",EDGE,"E0.sketch_text.stroke-23"),sQuery(id+"F0.wireOp",EDGE,"E0.sketch_text.stroke-25"),sQuery(id+"F0.wireOp",EDGE,"E0.sketch_text.stroke-26"),sQuery(id+"F0.wireOp",EDGE,"E0.sketch_text.stroke-27"),sQuery(id+"F0.wireOp",EDGE,"E0.sketch_text.stroke-28"),sQuery(id+"F0.wireOp",EDGE,"E0.sketch_text.stroke-29"),sQuery(id+"F0.wireOp",EDGE,"E0.sketch_text.stroke-30"),sQuery(id+"F0.wireOp",EDGE,"E0.sketch_text.stroke-31"),sQuery(id+"F0.wireOp",EDGE,"E0.sketch_text.stroke-33"),sQuery(id+"F0.wireOp",EDGE,"E0.sketch_text.stroke-34"),sQuery(id+"F0.wireOp",EDGE,"E0.sketch_text.stroke-35"),sQuery(id+"F0.wireOp",EDGE,"E0.sketch_text.stroke-36"),sQuery(id+"F0.wireOp",EDGE,"E0.sketch_text.stroke-37"),sQuery(id+"F0.wireOp",EDGE,"E0.sketch_text.stroke-38"),sQuery(id+"F0.wireOp",EDGE,"E0.sketch_text.stroke-39"),sQuery(id+"F0.wireOp",EDGE,"E0.sketch_text.stroke-40"),sQuery(id+"F0.wireOp",EDGE,"E0.sketch_text.stroke-41"),sQuery(id+"F0.wireOp",EDGE,"E0.sketch_text.stroke-42"),sQuery(id+"F0.wireOp",EDGE,"E0.sketch_text.stroke-43"),sQuery(id+"F0.wireOp",EDGE,"E1.bottom"),sQuery(id+"F0.wireOp",EDGE,"E1.top"),sQuery(id+"F0.wireOp",EDGE,"E7"),sQuery(id+"F0.wireOp",EDGE,"E8"),sQuery(id+"F0.wireOp",EDGE,"E9.MirrorCS"),sQuery(id+"F0.wireOp",EDGE,"E10.MirrorCS")])],"isStart":false})});
            var Q4;
            Q4=makeQuery(id+"F2.boolean.opBoolean","SPLIT",FACE,{"disambiguationData":[TD([makeQuery(id+"F2.opExtrude","SWEPT_FACE",FACE,{"disambiguationData":[OSD([sQuery(id+"F0.wireOp",EDGE,"E6.sketch_text.stroke-75")])]})])],"derivedFrom":makeQuery(id+"F1.opExtrude","CAP_FACE",FACE,{"disambiguationData":[OSD([sQuery(id+"F0.wireOp",EDGE,"E0.sketch_text.stroke-0"),sQuery(id+"F0.wireOp",EDGE,"E0.sketch_text.stroke-1"),sQuery(id+"F0.wireOp",EDGE,"E0.sketch_text.stroke-2"),sQuery(id+"F0.wireOp",EDGE,"E0.sketch_text.stroke-3"),sQuery(id+"F0.wireOp",EDGE,"E0.sketch_text.stroke-4"),sQuery(id+"F0.wireOp",EDGE,"E0.sketch_text.stroke-6"),sQuery(id+"F0.wireOp",EDGE,"E0.sketch_text.stroke-7"),sQuery(id+"F0.wireOp",EDGE,"E0.sketch_text.stroke-8"),sQuery(id+"F0.wireOp",EDGE,"E0.sketch_text.stroke-9"),sQuery(id+"F0.wireOp",EDGE,"E0.sketch_text.stroke-10"),sQuery(id+"F0.wireOp",EDGE,"E0.sketch_text.stroke-11"),sQuery(id+"F0.wireOp",EDGE,"E0.sketch_text.stroke-12"),sQuery(id+"F0.wireOp",EDGE,"E0.sketch_text.stroke-13"),sQuery(id+"F0.wireOp",EDGE,"E0.sketch_text.stroke-14"),sQuery(id+"F0.wireOp",EDGE,"E0.sketch_text.stroke-15"),sQuery(id+"F0.wireOp",EDGE,"E0.sketch_text.stroke-16"),sQuery(id+"F0.wireOp",EDGE,"E0.sketch_text.stroke-17"),sQuery(id+"F0.wireOp",EDGE,"E0.sketch_text.stroke-18"),sQuery(id+"F0.wireOp",EDGE,"E0.sketch_text.stroke-19"),sQuery(id+"F0.wireOp",EDGE,"E0.sketch_text.stroke-21"),sQuery(id+"F0.wireOp",EDGE,"E0.sketch_text.stroke-22"),sQuery(id+"F0.wireOp",EDGE,"E0.sketch_text.stroke-23"),sQuery(id+"F0.wireOp",EDGE,"E0.sketch_text.stroke-25"),sQuery(id+"F0.wireOp",EDGE,"E0.sketch_text.stroke-26"),sQuery(id+"F0.wireOp",EDGE,"E0.sketch_text.stroke-27"),sQuery(id+"F0.wireOp",EDGE,"E0.sketch_text.stroke-28"),sQuery(id+"F0.wireOp",EDGE,"E0.sketch_text.stroke-29"),sQuery(id+"F0.wireOp",EDGE,"E0.sketch_text.stroke-30"),sQuery(id+"F0.wireOp",EDGE,"E0.sketch_text.stroke-31"),sQuery(id+"F0.wireOp",EDGE,"E0.sketch_text.stroke-33"),sQuery(id+"F0.wireOp",EDGE,"E0.sketch_text.stroke-34"),sQuery(id+"F0.wireOp",EDGE,"E0.sketch_text.stroke-35"),sQuery(id+"F0.wireOp",EDGE,"E0.sketch_text.stroke-36"),sQuery(id+"F0.wireOp",EDGE,"E0.sketch_text.stroke-37"),sQuery(id+"F0.wireOp",EDGE,"E0.sketch_text.stroke-38"),sQuery(id+"F0.wireOp",EDGE,"E0.sketch_text.stroke-39"),sQuery(id+"F0.wireOp",EDGE,"E0.sketch_text.stroke-40"),sQuery(id+"F0.wireOp",EDGE,"E0.sketch_text.stroke-41"),sQuery(id+"F0.wireOp",EDGE,"E0.sketch_text.stroke-42"),sQuery(id+"F0.wireOp",EDGE,"E0.sketch_text.stroke-43"),sQuery(id+"F0.wireOp",EDGE,"E1.bottom"),sQuery(id+"F0.wireOp",EDGE,"E1.top"),sQuery(id+"F0.wireOp",EDGE,"E7"),sQuery(id+"F0.wireOp",EDGE,"E8"),sQuery(id+"F0.wireOp",EDGE,"E9.MirrorCS"),sQuery(id+"F0.wireOp",EDGE,"E10.MirrorCS")])],"isStart":false})});
            var Q5;
            Q5=makeQuery(id+"F2.boolean.opBoolean","COPY",FACE,{"derivedFrom":makeQuery(id+"F2.opExtrude","CAP_FACE",FACE,{"disambiguationData":[OSD([sQuery(id+"F0.wireOp",EDGE,"E6.sketch_text.stroke-12"),sQuery(id+"F0.wireOp",EDGE,"E6.sketch_text.stroke-13"),sQuery(id+"F0.wireOp",EDGE,"E6.sketch_text.stroke-14"),sQuery(id+"F0.wireOp",EDGE,"E6.sketch_text.stroke-15"),sQuery(id+"F0.wireOp",EDGE,"E6.sketch_text.stroke-16"),sQuery(id+"F0.wireOp",EDGE,"E6.sketch_text.stroke-17"),sQuery(id+"F0.wireOp",EDGE,"E6.sketch_text.stroke-18"),sQuery(id+"F0.wireOp",EDGE,"E6.sketch_text.stroke-19"),sQuery(id+"F0.wireOp",EDGE,"E6.sketch_text.stroke-20"),sQuery(id+"F0.wireOp",EDGE,"E6.sketch_text.stroke-21"),sQuery(id+"F0.wireOp",EDGE,"E6.sketch_text.stroke-22"),sQuery(id+"F0.wireOp",EDGE,"E6.sketch_text.stroke-23"),sQuery(id+"F0.wireOp",EDGE,"E6.sketch_text.stroke-24"),sQuery(id+"F0.wireOp",EDGE,"E6.sketch_text.stroke-25"),sQuery(id+"F0.wireOp",EDGE,"E6.sketch_text.stroke-26"),sQuery(id+"F0.wireOp",EDGE,"E6.sketch_text.stroke-27"),sQuery(id+"F0.wireOp",EDGE,"E6.sketch_text.stroke-28")])],"isStart":true})});
            var Q6;
            Q6=makeQuery(id+"F2.boolean.opBoolean","COPY",FACE,{"derivedFrom":makeQuery(id+"F2.opExtrude","CAP_FACE",FACE,{"disambiguationData":[OSD([sQuery(id+"F0.wireOp",EDGE,"E6.sketch_text.stroke-0"),sQuery(id+"F0.wireOp",EDGE,"E6.sketch_text.stroke-1"),sQuery(id+"F0.wireOp",EDGE,"E6.sketch_text.stroke-2"),sQuery(id+"F0.wireOp",EDGE,"E6.sketch_text.stroke-3"),sQuery(id+"F0.wireOp",EDGE,"E6.sketch_text.stroke-4"),sQuery(id+"F0.wireOp",EDGE,"E6.sketch_text.stroke-5"),sQuery(id+"F0.wireOp",EDGE,"E6.sketch_text.stroke-6"),sQuery(id+"F0.wireOp",EDGE,"E6.sketch_text.stroke-7"),sQuery(id+"F0.wireOp",EDGE,"E6.sketch_text.stroke-8"),sQuery(id+"F0.wireOp",EDGE,"E6.sketch_text.stroke-9"),sQuery(id+"F0.wireOp",EDGE,"E6.sketch_text.stroke-10"),sQuery(id+"F0.wireOp",EDGE,"E6.sketch_text.stroke-11")])],"isStart":true})});
            var Q7;
            Q7=makeQuery(id+"F2.boolean.opBoolean","COPY",FACE,{"derivedFrom":makeQuery(id+"F2.opExtrude","CAP_FACE",FACE,{"disambiguationData":[OSD([sQuery(id+"F0.wireOp",EDGE,"E6.sketch_text.stroke-29"),sQuery(id+"F0.wireOp",EDGE,"E6.sketch_text.stroke-30"),sQuery(id+"F0.wireOp",EDGE,"E6.sketch_text.stroke-31"),sQuery(id+"F0.wireOp",EDGE,"E6.sketch_text.stroke-32"),sQuery(id+"F0.wireOp",EDGE,"E6.sketch_text.stroke-33"),sQuery(id+"F0.wireOp",EDGE,"E6.sketch_text.stroke-34"),sQuery(id+"F0.wireOp",EDGE,"E6.sketch_text.stroke-35"),sQuery(id+"F0.wireOp",EDGE,"E6.sketch_text.stroke-36"),sQuery(id+"F0.wireOp",EDGE,"E6.sketch_text.stroke-37"),sQuery(id+"F0.wireOp",EDGE,"E6.sketch_text.stroke-38"),sQuery(id+"F0.wireOp",EDGE,"E6.sketch_text.stroke-39"),sQuery(id+"F0.wireOp",EDGE,"E6.sketch_text.stroke-40"),sQuery(id+"F0.wireOp",EDGE,"E6.sketch_text.stroke-41"),sQuery(id+"F0.wireOp",EDGE,"E6.sketch_text.stroke-42"),sQuery(id+"F0.wireOp",EDGE,"E6.sketch_text.stroke-43"),sQuery(id+"F0.wireOp",EDGE,"E6.sketch_text.stroke-44"),sQuery(id+"F0.wireOp",EDGE,"E6.sketch_text.stroke-45")])],"isStart":true})});
            var Q8;
            Q8=makeQuery(id+"F2.boolean.opBoolean","COPY",FACE,{"derivedFrom":makeQuery(id+"F2.opExtrude","CAP_FACE",FACE,{"disambiguationData":[OSD([sQuery(id+"F0.wireOp",EDGE,"E6.sketch_text.stroke-46"),sQuery(id+"F0.wireOp",EDGE,"E6.sketch_text.stroke-47"),sQuery(id+"F0.wireOp",EDGE,"E6.sketch_text.stroke-48"),sQuery(id+"F0.wireOp",EDGE,"E6.sketch_text.stroke-49"),sQuery(id+"F0.wireOp",EDGE,"E6.sketch_text.stroke-50"),sQuery(id+"F0.wireOp",EDGE,"E6.sketch_text.stroke-51"),sQuery(id+"F0.wireOp",EDGE,"E6.sketch_text.stroke-52"),sQuery(id+"F0.wireOp",EDGE,"E6.sketch_text.stroke-53"),sQuery(id+"F0.wireOp",EDGE,"E6.sketch_text.stroke-54"),sQuery(id+"F0.wireOp",EDGE,"E6.sketch_text.stroke-55"),sQuery(id+"F0.wireOp",EDGE,"E6.sketch_text.stroke-56"),sQuery(id+"F0.wireOp",EDGE,"E6.sketch_text.stroke-57"),sQuery(id+"F0.wireOp",EDGE,"E6.sketch_text.stroke-58"),sQuery(id+"F0.wireOp",EDGE,"E6.sketch_text.stroke-59"),sQuery(id+"F0.wireOp",EDGE,"E6.sketch_text.stroke-60"),sQuery(id+"F0.wireOp",EDGE,"E6.sketch_text.stroke-61"),sQuery(id+"F0.wireOp",EDGE,"E6.sketch_text.stroke-62"),sQuery(id+"F0.wireOp",EDGE,"E6.sketch_text.stroke-63"),sQuery(id+"F0.wireOp",EDGE,"E6.sketch_text.stroke-64"),sQuery(id+"F0.wireOp",EDGE,"E6.sketch_text.stroke-65"),sQuery(id+"F0.wireOp",EDGE,"E6.sketch_text.stroke-66"),sQuery(id+"F0.wireOp",EDGE,"E6.sketch_text.stroke-67"),sQuery(id+"F0.wireOp",EDGE,"E6.sketch_text.stroke-68"),sQuery(id+"F0.wireOp",EDGE,"E6.sketch_text.stroke-69"),sQuery(id+"F0.wireOp",EDGE,"E6.sketch_text.stroke-70"),sQuery(id+"F0.wireOp",EDGE,"E6.sketch_text.stroke-71"),sQuery(id+"F0.wireOp",EDGE,"E6.sketch_text.stroke-72"),sQuery(id+"F0.wireOp",EDGE,"E6.sketch_text.stroke-73"),sQuery(id+"F0.wireOp",EDGE,"E6.sketch_text.stroke-74"),sQuery(id+"F0.wireOp",EDGE,"E6.sketch_text.stroke-75"),sQuery(id+"F0.wireOp",EDGE,"E6.sketch_text.stroke-76"),sQuery(id+"F0.wireOp",EDGE,"E6.sketch_text.stroke-77"),sQuery(id+"F0.wireOp",EDGE,"E6.sketch_text.stroke-78"),sQuery(id+"F0.wireOp",EDGE,"E6.sketch_text.stroke-79"),sQuery(id+"F0.wireOp",EDGE,"E6.sketch_text.stroke-80"),sQuery(id+"F0.wireOp",EDGE,"E6.sketch_text.stroke-81"),sQuery(id+"F0.wireOp",EDGE,"E6.sketch_text.stroke-82"),sQuery(id+"F0.wireOp",EDGE,"E6.sketch_text.stroke-83"),sQuery(id+"F0.wireOp",EDGE,"E6.sketch_text.stroke-84"),sQuery(id+"F0.wireOp",EDGE,"E6.sketch_text.stroke-85"),sQuery(id+"F0.wireOp",EDGE,"E6.sketch_text.stroke-86"),sQuery(id+"F0.wireOp",EDGE,"E6.sketch_text.stroke-87"),sQuery(id+"F0.wireOp",EDGE,"E6.sketch_text.stroke-88"),sQuery(id+"F0.wireOp",EDGE,"E6.sketch_text.stroke-89")])],"isStart":true})});
            var Q9;
            Q9=makeQuery(id+"F2.boolean.opBoolean","SPLIT",FACE,{"disambiguationData":[TD([makeQuery(id+"F2.opExtrude","SWEPT_FACE",FACE,{"disambiguationData":[OSD([sQuery(id+"F0.wireOp",EDGE,"E6.sketch_text.stroke-104")])]})])],"derivedFrom":makeQuery(id+"F1.opExtrude","CAP_FACE",FACE,{"disambiguationData":[OSD([sQuery(id+"F0.wireOp",EDGE,"E0.sketch_text.stroke-0"),sQuery(id+"F0.wireOp",EDGE,"E0.sketch_text.stroke-1"),sQuery(id+"F0.wireOp",EDGE,"E0.sketch_text.stroke-2"),sQuery(id+"F0.wireOp",EDGE,"E0.sketch_text.stroke-3"),sQuery(id+"F0.wireOp",EDGE,"E0.sketch_text.stroke-4"),sQuery(id+"F0.wireOp",EDGE,"E0.sketch_text.stroke-6"),sQuery(id+"F0.wireOp",EDGE,"E0.sketch_text.stroke-7"),sQuery(id+"F0.wireOp",EDGE,"E0.sketch_text.stroke-8"),sQuery(id+"F0.wireOp",EDGE,"E0.sketch_text.stroke-9"),sQuery(id+"F0.wireOp",EDGE,"E0.sketch_text.stroke-10"),sQuery(id+"F0.wireOp",EDGE,"E0.sketch_text.stroke-11"),sQuery(id+"F0.wireOp",EDGE,"E0.sketch_text.stroke-12"),sQuery(id+"F0.wireOp",EDGE,"E0.sketch_text.stroke-13"),sQuery(id+"F0.wireOp",EDGE,"E0.sketch_text.stroke-14"),sQuery(id+"F0.wireOp",EDGE,"E0.sketch_text.stroke-15"),sQuery(id+"F0.wireOp",EDGE,"E0.sketch_text.stroke-16"),sQuery(id+"F0.wireOp",EDGE,"E0.sketch_text.stroke-17"),sQuery(id+"F0.wireOp",EDGE,"E0.sketch_text.stroke-18"),sQuery(id+"F0.wireOp",EDGE,"E0.sketch_text.stroke-19"),sQuery(id+"F0.wireOp",EDGE,"E0.sketch_text.stroke-21"),sQuery(id+"F0.wireOp",EDGE,"E0.sketch_text.stroke-22"),sQuery(id+"F0.wireOp",EDGE,"E0.sketch_text.stroke-23"),sQuery(id+"F0.wireOp",EDGE,"E0.sketch_text.stroke-25"),sQuery(id+"F0.wireOp",EDGE,"E0.sketch_text.stroke-26"),sQuery(id+"F0.wireOp",EDGE,"E0.sketch_text.stroke-27"),sQuery(id+"F0.wireOp",EDGE,"E0.sketch_text.stroke-28"),sQuery(id+"F0.wireOp",EDGE,"E0.sketch_text.stroke-29"),sQuery(id+"F0.wireOp",EDGE,"E0.sketch_text.stroke-30"),sQuery(id+"F0.wireOp",EDGE,"E0.sketch_text.stroke-31"),sQuery(id+"F0.wireOp",EDGE,"E0.sketch_text.stroke-33"),sQuery(id+"F0.wireOp",EDGE,"E0.sketch_text.stroke-34"),sQuery(id+"F0.wireOp",EDGE,"E0.sketch_text.stroke-35"),sQuery(id+"F0.wireOp",EDGE,"E0.sketch_text.stroke-36"),sQuery(id+"F0.wireOp",EDGE,"E0.sketch_text.stroke-37"),sQuery(id+"F0.wireOp",EDGE,"E0.sketch_text.stroke-38"),sQuery(id+"F0.wireOp",EDGE,"E0.sketch_text.stroke-39"),sQuery(id+"F0.wireOp",EDGE,"E0.sketch_text.stroke-40"),sQuery(id+"F0.wireOp",EDGE,"E0.sketch_text.stroke-41"),sQuery(id+"F0.wireOp",EDGE,"E0.sketch_text.stroke-42"),sQuery(id+"F0.wireOp",EDGE,"E0.sketch_text.stroke-43"),sQuery(id+"F0.wireOp",EDGE,"E1.bottom"),sQuery(id+"F0.wireOp",EDGE,"E1.top"),sQuery(id+"F0.wireOp",EDGE,"E7"),sQuery(id+"F0.wireOp",EDGE,"E8"),sQuery(id+"F0.wireOp",EDGE,"E9.MirrorCS"),sQuery(id+"F0.wireOp",EDGE,"E10.MirrorCS")])],"isStart":false})});
            var Q10;
            Q10=makeQuery(id+"F2.boolean.opBoolean","COPY",FACE,{"derivedFrom":makeQuery(id+"F2.opExtrude","CAP_FACE",FACE,{"disambiguationData":[OSD([sQuery(id+"F0.wireOp",EDGE,"E6.sketch_text.stroke-90"),sQuery(id+"F0.wireOp",EDGE,"E6.sketch_text.stroke-91"),sQuery(id+"F0.wireOp",EDGE,"E6.sketch_text.stroke-92"),sQuery(id+"F0.wireOp",EDGE,"E6.sketch_text.stroke-93"),sQuery(id+"F0.wireOp",EDGE,"E6.sketch_text.stroke-94"),sQuery(id+"F0.wireOp",EDGE,"E6.sketch_text.stroke-95"),sQuery(id+"F0.wireOp",EDGE,"E6.sketch_text.stroke-96"),sQuery(id+"F0.wireOp",EDGE,"E6.sketch_text.stroke-97"),sQuery(id+"F0.wireOp",EDGE,"E6.sketch_text.stroke-98"),sQuery(id+"F0.wireOp",EDGE,"E6.sketch_text.stroke-99"),sQuery(id+"F0.wireOp",EDGE,"E6.sketch_text.stroke-100"),sQuery(id+"F0.wireOp",EDGE,"E6.sketch_text.stroke-101"),sQuery(id+"F0.wireOp",EDGE,"E6.sketch_text.stroke-102"),sQuery(id+"F0.wireOp",EDGE,"E6.sketch_text.stroke-103"),sQuery(id+"F0.wireOp",EDGE,"E6.sketch_text.stroke-104"),sQuery(id+"F0.wireOp",EDGE,"E6.sketch_text.stroke-105"),sQuery(id+"F0.wireOp",EDGE,"E6.sketch_text.stroke-106"),sQuery(id+"F0.wireOp",EDGE,"E6.sketch_text.stroke-107"),sQuery(id+"F0.wireOp",EDGE,"E6.sketch_text.stroke-108")])],"isStart":true})});
            var Q11;
            Q11=makeQuery(id+"F2.boolean.opBoolean","COPY",FACE,{"derivedFrom":makeQuery(id+"F2.opExtrude","CAP_FACE",FACE,{"disambiguationData":[OSD([sQuery(id+"F0.wireOp",EDGE,"E6.sketch_text.stroke-109"),sQuery(id+"F0.wireOp",EDGE,"E6.sketch_text.stroke-110"),sQuery(id+"F0.wireOp",EDGE,"E6.sketch_text.stroke-111"),sQuery(id+"F0.wireOp",EDGE,"E6.sketch_text.stroke-112"),sQuery(id+"F0.wireOp",EDGE,"E6.sketch_text.stroke-113"),sQuery(id+"F0.wireOp",EDGE,"E6.sketch_text.stroke-114"),sQuery(id+"F0.wireOp",EDGE,"E6.sketch_text.stroke-115"),sQuery(id+"F0.wireOp",EDGE,"E6.sketch_text.stroke-116"),sQuery(id+"F0.wireOp",EDGE,"E6.sketch_text.stroke-117"),sQuery(id+"F0.wireOp",EDGE,"E6.sketch_text.stroke-118"),sQuery(id+"F0.wireOp",EDGE,"E6.sketch_text.stroke-119"),sQuery(id+"F0.wireOp",EDGE,"E6.sketch_text.stroke-120"),sQuery(id+"F0.wireOp",EDGE,"E6.sketch_text.stroke-121"),sQuery(id+"F0.wireOp",EDGE,"E6.sketch_text.stroke-122"),sQuery(id+"F0.wireOp",EDGE,"E6.sketch_text.stroke-123"),sQuery(id+"F0.wireOp",EDGE,"E6.sketch_text.stroke-124"),sQuery(id+"F0.wireOp",EDGE,"E6.sketch_text.stroke-125")])],"isStart":true})});
            var Q12;
            Q12=makeQuery(id+"F2.boolean.opBoolean","SPLIT",FACE,{"disambiguationData":[TD([makeQuery(id+"F2.opExtrude","SWEPT_FACE",FACE,{"disambiguationData":[OSD([sQuery(id+"F0.wireOp",EDGE,"E6.sketch_text.stroke-141")])]})])],"derivedFrom":makeQuery(id+"F1.opExtrude","CAP_FACE",FACE,{"disambiguationData":[OSD([sQuery(id+"F0.wireOp",EDGE,"E0.sketch_text.stroke-0"),sQuery(id+"F0.wireOp",EDGE,"E0.sketch_text.stroke-1"),sQuery(id+"F0.wireOp",EDGE,"E0.sketch_text.stroke-2"),sQuery(id+"F0.wireOp",EDGE,"E0.sketch_text.stroke-3"),sQuery(id+"F0.wireOp",EDGE,"E0.sketch_text.stroke-4"),sQuery(id+"F0.wireOp",EDGE,"E0.sketch_text.stroke-6"),sQuery(id+"F0.wireOp",EDGE,"E0.sketch_text.stroke-7"),sQuery(id+"F0.wireOp",EDGE,"E0.sketch_text.stroke-8"),sQuery(id+"F0.wireOp",EDGE,"E0.sketch_text.stroke-9"),sQuery(id+"F0.wireOp",EDGE,"E0.sketch_text.stroke-10"),sQuery(id+"F0.wireOp",EDGE,"E0.sketch_text.stroke-11"),sQuery(id+"F0.wireOp",EDGE,"E0.sketch_text.stroke-12"),sQuery(id+"F0.wireOp",EDGE,"E0.sketch_text.stroke-13"),sQuery(id+"F0.wireOp",EDGE,"E0.sketch_text.stroke-14"),sQuery(id+"F0.wireOp",EDGE,"E0.sketch_text.stroke-15"),sQuery(id+"F0.wireOp",EDGE,"E0.sketch_text.stroke-16"),sQuery(id+"F0.wireOp",EDGE,"E0.sketch_text.stroke-17"),sQuery(id+"F0.wireOp",EDGE,"E0.sketch_text.stroke-18"),sQuery(id+"F0.wireOp",EDGE,"E0.sketch_text.stroke-19"),sQuery(id+"F0.wireOp",EDGE,"E0.sketch_text.stroke-21"),sQuery(id+"F0.wireOp",EDGE,"E0.sketch_text.stroke-22"),sQuery(id+"F0.wireOp",EDGE,"E0.sketch_text.stroke-23"),sQuery(id+"F0.wireOp",EDGE,"E0.sketch_text.stroke-25"),sQuery(id+"F0.wireOp",EDGE,"E0.sketch_text.stroke-26"),sQuery(id+"F0.wireOp",EDGE,"E0.sketch_text.stroke-27"),sQuery(id+"F0.wireOp",EDGE,"E0.sketch_text.stroke-28"),sQuery(id+"F0.wireOp",EDGE,"E0.sketch_text.stroke-29"),sQuery(id+"F0.wireOp",EDGE,"E0.sketch_text.stroke-30"),sQuery(id+"F0.wireOp",EDGE,"E0.sketch_text.stroke-31"),sQuery(id+"F0.wireOp",EDGE,"E0.sketch_text.stroke-33"),sQuery(id+"F0.wireOp",EDGE,"E0.sketch_text.stroke-34"),sQuery(id+"F0.wireOp",EDGE,"E0.sketch_text.stroke-35"),sQuery(id+"F0.wireOp",EDGE,"E0.sketch_text.stroke-36"),sQuery(id+"F0.wireOp",EDGE,"E0.sketch_text.stroke-37"),sQuery(id+"F0.wireOp",EDGE,"E0.sketch_text.stroke-38"),sQuery(id+"F0.wireOp",EDGE,"E0.sketch_text.stroke-39"),sQuery(id+"F0.wireOp",EDGE,"E0.sketch_text.stroke-40"),sQuery(id+"F0.wireOp",EDGE,"E0.sketch_text.stroke-41"),sQuery(id+"F0.wireOp",EDGE,"E0.sketch_text.stroke-42"),sQuery(id+"F0.wireOp",EDGE,"E0.sketch_text.stroke-43"),sQuery(id+"F0.wireOp",EDGE,"E1.bottom"),sQuery(id+"F0.wireOp",EDGE,"E1.top"),sQuery(id+"F0.wireOp",EDGE,"E7"),sQuery(id+"F0.wireOp",EDGE,"E8"),sQuery(id+"F0.wireOp",EDGE,"E9.MirrorCS"),sQuery(id+"F0.wireOp",EDGE,"E10.MirrorCS")])],"isStart":false})});
            var Q13;
            Q13=makeQuery(id+"F2.boolean.opBoolean","SPLIT",FACE,{"disambiguationData":[TD([makeQuery(id+"F2.opExtrude","SWEPT_FACE",FACE,{"disambiguationData":[OSD([sQuery(id+"F0.wireOp",EDGE,"E6.sketch_text.stroke-159")])]})])],"derivedFrom":makeQuery(id+"F1.opExtrude","CAP_FACE",FACE,{"disambiguationData":[OSD([sQuery(id+"F0.wireOp",EDGE,"E0.sketch_text.stroke-0"),sQuery(id+"F0.wireOp",EDGE,"E0.sketch_text.stroke-1"),sQuery(id+"F0.wireOp",EDGE,"E0.sketch_text.stroke-2"),sQuery(id+"F0.wireOp",EDGE,"E0.sketch_text.stroke-3"),sQuery(id+"F0.wireOp",EDGE,"E0.sketch_text.stroke-4"),sQuery(id+"F0.wireOp",EDGE,"E0.sketch_text.stroke-6"),sQuery(id+"F0.wireOp",EDGE,"E0.sketch_text.stroke-7"),sQuery(id+"F0.wireOp",EDGE,"E0.sketch_text.stroke-8"),sQuery(id+"F0.wireOp",EDGE,"E0.sketch_text.stroke-9"),sQuery(id+"F0.wireOp",EDGE,"E0.sketch_text.stroke-10"),sQuery(id+"F0.wireOp",EDGE,"E0.sketch_text.stroke-11"),sQuery(id+"F0.wireOp",EDGE,"E0.sketch_text.stroke-12"),sQuery(id+"F0.wireOp",EDGE,"E0.sketch_text.stroke-13"),sQuery(id+"F0.wireOp",EDGE,"E0.sketch_text.stroke-14"),sQuery(id+"F0.wireOp",EDGE,"E0.sketch_text.stroke-15"),sQuery(id+"F0.wireOp",EDGE,"E0.sketch_text.stroke-16"),sQuery(id+"F0.wireOp",EDGE,"E0.sketch_text.stroke-17"),sQuery(id+"F0.wireOp",EDGE,"E0.sketch_text.stroke-18"),sQuery(id+"F0.wireOp",EDGE,"E0.sketch_text.stroke-19"),sQuery(id+"F0.wireOp",EDGE,"E0.sketch_text.stroke-21"),sQuery(id+"F0.wireOp",EDGE,"E0.sketch_text.stroke-22"),sQuery(id+"F0.wireOp",EDGE,"E0.sketch_text.stroke-23"),sQuery(id+"F0.wireOp",EDGE,"E0.sketch_text.stroke-25"),sQuery(id+"F0.wireOp",EDGE,"E0.sketch_text.stroke-26"),sQuery(id+"F0.wireOp",EDGE,"E0.sketch_text.stroke-27"),sQuery(id+"F0.wireOp",EDGE,"E0.sketch_text.stroke-28"),sQuery(id+"F0.wireOp",EDGE,"E0.sketch_text.stroke-29"),sQuery(id+"F0.wireOp",EDGE,"E0.sketch_text.stroke-30"),sQuery(id+"F0.wireOp",EDGE,"E0.sketch_text.stroke-31"),sQuery(id+"F0.wireOp",EDGE,"E0.sketch_text.stroke-33"),sQuery(id+"F0.wireOp",EDGE,"E0.sketch_text.stroke-34"),sQuery(id+"F0.wireOp",EDGE,"E0.sketch_text.stroke-35"),sQuery(id+"F0.wireOp",EDGE,"E0.sketch_text.stroke-36"),sQuery(id+"F0.wireOp",EDGE,"E0.sketch_text.stroke-37"),sQuery(id+"F0.wireOp",EDGE,"E0.sketch_text.stroke-38"),sQuery(id+"F0.wireOp",EDGE,"E0.sketch_text.stroke-39"),sQuery(id+"F0.wireOp",EDGE,"E0.sketch_text.stroke-40"),sQuery(id+"F0.wireOp",EDGE,"E0.sketch_text.stroke-41"),sQuery(id+"F0.wireOp",EDGE,"E0.sketch_text.stroke-42"),sQuery(id+"F0.wireOp",EDGE,"E0.sketch_text.stroke-43"),sQuery(id+"F0.wireOp",EDGE,"E1.bottom"),sQuery(id+"F0.wireOp",EDGE,"E1.top"),sQuery(id+"F0.wireOp",EDGE,"E7"),sQuery(id+"F0.wireOp",EDGE,"E8"),sQuery(id+"F0.wireOp",EDGE,"E9.MirrorCS"),sQuery(id+"F0.wireOp",EDGE,"E10.MirrorCS")])],"isStart":false})});
            var Q14;
            Q14=makeQuery(id+"F2.boolean.opBoolean","SPLIT",FACE,{"disambiguationData":[TD([makeQuery(id+"F2.opExtrude","SWEPT_FACE",FACE,{"disambiguationData":[OSD([sQuery(id+"F0.wireOp",EDGE,"E6.sketch_text.stroke-176")])]})])],"derivedFrom":makeQuery(id+"F1.opExtrude","CAP_FACE",FACE,{"disambiguationData":[OSD([sQuery(id+"F0.wireOp",EDGE,"E0.sketch_text.stroke-0"),sQuery(id+"F0.wireOp",EDGE,"E0.sketch_text.stroke-1"),sQuery(id+"F0.wireOp",EDGE,"E0.sketch_text.stroke-2"),sQuery(id+"F0.wireOp",EDGE,"E0.sketch_text.stroke-3"),sQuery(id+"F0.wireOp",EDGE,"E0.sketch_text.stroke-4"),sQuery(id+"F0.wireOp",EDGE,"E0.sketch_text.stroke-6"),sQuery(id+"F0.wireOp",EDGE,"E0.sketch_text.stroke-7"),sQuery(id+"F0.wireOp",EDGE,"E0.sketch_text.stroke-8"),sQuery(id+"F0.wireOp",EDGE,"E0.sketch_text.stroke-9"),sQuery(id+"F0.wireOp",EDGE,"E0.sketch_text.stroke-10"),sQuery(id+"F0.wireOp",EDGE,"E0.sketch_text.stroke-11"),sQuery(id+"F0.wireOp",EDGE,"E0.sketch_text.stroke-12"),sQuery(id+"F0.wireOp",EDGE,"E0.sketch_text.stroke-13"),sQuery(id+"F0.wireOp",EDGE,"E0.sketch_text.stroke-14"),sQuery(id+"F0.wireOp",EDGE,"E0.sketch_text.stroke-15"),sQuery(id+"F0.wireOp",EDGE,"E0.sketch_text.stroke-16"),sQuery(id+"F0.wireOp",EDGE,"E0.sketch_text.stroke-17"),sQuery(id+"F0.wireOp",EDGE,"E0.sketch_text.stroke-18"),sQuery(id+"F0.wireOp",EDGE,"E0.sketch_text.stroke-19"),sQuery(id+"F0.wireOp",EDGE,"E0.sketch_text.stroke-21"),sQuery(id+"F0.wireOp",EDGE,"E0.sketch_text.stroke-22"),sQuery(id+"F0.wireOp",EDGE,"E0.sketch_text.stroke-23"),sQuery(id+"F0.wireOp",EDGE,"E0.sketch_text.stroke-25"),sQuery(id+"F0.wireOp",EDGE,"E0.sketch_text.stroke-26"),sQuery(id+"F0.wireOp",EDGE,"E0.sketch_text.stroke-27"),sQuery(id+"F0.wireOp",EDGE,"E0.sketch_text.stroke-28"),sQuery(id+"F0.wireOp",EDGE,"E0.sketch_text.stroke-29"),sQuery(id+"F0.wireOp",EDGE,"E0.sketch_text.stroke-30"),sQuery(id+"F0.wireOp",EDGE,"E0.sketch_text.stroke-31"),sQuery(id+"F0.wireOp",EDGE,"E0.sketch_text.stroke-33"),sQuery(id+"F0.wireOp",EDGE,"E0.sketch_text.stroke-34"),sQuery(id+"F0.wireOp",EDGE,"E0.sketch_text.stroke-35"),sQuery(id+"F0.wireOp",EDGE,"E0.sketch_text.stroke-36"),sQuery(id+"F0.wireOp",EDGE,"E0.sketch_text.stroke-37"),sQuery(id+"F0.wireOp",EDGE,"E0.sketch_text.stroke-38"),sQuery(id+"F0.wireOp",EDGE,"E0.sketch_text.stroke-39"),sQuery(id+"F0.wireOp",EDGE,"E0.sketch_text.stroke-40"),sQuery(id+"F0.wireOp",EDGE,"E0.sketch_text.stroke-41"),sQuery(id+"F0.wireOp",EDGE,"E0.sketch_text.stroke-42"),sQuery(id+"F0.wireOp",EDGE,"E0.sketch_text.stroke-43"),sQuery(id+"F0.wireOp",EDGE,"E1.bottom"),sQuery(id+"F0.wireOp",EDGE,"E1.top"),sQuery(id+"F0.wireOp",EDGE,"E7"),sQuery(id+"F0.wireOp",EDGE,"E8"),sQuery(id+"F0.wireOp",EDGE,"E9.MirrorCS"),sQuery(id+"F0.wireOp",EDGE,"E10.MirrorCS")])],"isStart":false})});
            var Q15;
            Q15=makeQuery(id+"F2.boolean.opBoolean","COPY",FACE,{"derivedFrom":makeQuery(id+"F2.opExtrude","CAP_FACE",FACE,{"disambiguationData":[OSD([sQuery(id+"F0.wireOp",EDGE,"E6.sketch_text.stroke-126"),sQuery(id+"F0.wireOp",EDGE,"E6.sketch_text.stroke-127"),sQuery(id+"F0.wireOp",EDGE,"E6.sketch_text.stroke-128"),sQuery(id+"F0.wireOp",EDGE,"E6.sketch_text.stroke-129"),sQuery(id+"F0.wireOp",EDGE,"E6.sketch_text.stroke-130"),sQuery(id+"F0.wireOp",EDGE,"E6.sketch_text.stroke-131"),sQuery(id+"F0.wireOp",EDGE,"E6.sketch_text.stroke-132"),sQuery(id+"F0.wireOp",EDGE,"E6.sketch_text.stroke-133"),sQuery(id+"F0.wireOp",EDGE,"E6.sketch_text.stroke-134"),sQuery(id+"F0.wireOp",EDGE,"E6.sketch_text.stroke-135"),sQuery(id+"F0.wireOp",EDGE,"E6.sketch_text.stroke-136"),sQuery(id+"F0.wireOp",EDGE,"E6.sketch_text.stroke-137"),sQuery(id+"F0.wireOp",EDGE,"E6.sketch_text.stroke-138"),sQuery(id+"F0.wireOp",EDGE,"E6.sketch_text.stroke-139"),sQuery(id+"F0.wireOp",EDGE,"E6.sketch_text.stroke-140"),sQuery(id+"F0.wireOp",EDGE,"E6.sketch_text.stroke-141"),sQuery(id+"F0.wireOp",EDGE,"E6.sketch_text.stroke-142"),sQuery(id+"F0.wireOp",EDGE,"E6.sketch_text.stroke-143"),sQuery(id+"F0.wireOp",EDGE,"E6.sketch_text.stroke-144"),sQuery(id+"F0.wireOp",EDGE,"E6.sketch_text.stroke-145"),sQuery(id+"F0.wireOp",EDGE,"E6.sketch_text.stroke-146"),sQuery(id+"F0.wireOp",EDGE,"E6.sketch_text.stroke-147"),sQuery(id+"F0.wireOp",EDGE,"E6.sketch_text.stroke-148"),sQuery(id+"F0.wireOp",EDGE,"E6.sketch_text.stroke-149")])],"isStart":true})});
            var Q16;
            Q16=makeQuery(id+"F2.boolean.opBoolean","COPY",FACE,{"derivedFrom":makeQuery(id+"F2.opExtrude","CAP_FACE",FACE,{"disambiguationData":[OSD([sQuery(id+"F0.wireOp",EDGE,"E6.sketch_text.stroke-150"),sQuery(id+"F0.wireOp",EDGE,"E6.sketch_text.stroke-151"),sQuery(id+"F0.wireOp",EDGE,"E6.sketch_text.stroke-152"),sQuery(id+"F0.wireOp",EDGE,"E6.sketch_text.stroke-153"),sQuery(id+"F0.wireOp",EDGE,"E6.sketch_text.stroke-154"),sQuery(id+"F0.wireOp",EDGE,"E6.sketch_text.stroke-155"),sQuery(id+"F0.wireOp",EDGE,"E6.sketch_text.stroke-156"),sQuery(id+"F0.wireOp",EDGE,"E6.sketch_text.stroke-157"),sQuery(id+"F0.wireOp",EDGE,"E6.sketch_text.stroke-158"),sQuery(id+"F0.wireOp",EDGE,"E6.sketch_text.stroke-159"),sQuery(id+"F0.wireOp",EDGE,"E6.sketch_text.stroke-160"),sQuery(id+"F0.wireOp",EDGE,"E6.sketch_text.stroke-161"),sQuery(id+"F0.wireOp",EDGE,"E6.sketch_text.stroke-162"),sQuery(id+"F0.wireOp",EDGE,"E6.sketch_text.stroke-163"),sQuery(id+"F0.wireOp",EDGE,"E6.sketch_text.stroke-164"),sQuery(id+"F0.wireOp",EDGE,"E6.sketch_text.stroke-165"),sQuery(id+"F0.wireOp",EDGE,"E6.sketch_text.stroke-166")])],"isStart":true})});
            var Q17;
            Q17=makeQuery(id+"F2.boolean.opBoolean","COPY",FACE,{"derivedFrom":makeQuery(id+"F2.opExtrude","CAP_FACE",FACE,{"disambiguationData":[OSD([sQuery(id+"F0.wireOp",EDGE,"E6.sketch_text.stroke-167"),sQuery(id+"F0.wireOp",EDGE,"E6.sketch_text.stroke-168"),sQuery(id+"F0.wireOp",EDGE,"E6.sketch_text.stroke-169"),sQuery(id+"F0.wireOp",EDGE,"E6.sketch_text.stroke-170"),sQuery(id+"F0.wireOp",EDGE,"E6.sketch_text.stroke-171"),sQuery(id+"F0.wireOp",EDGE,"E6.sketch_text.stroke-172"),sQuery(id+"F0.wireOp",EDGE,"E6.sketch_text.stroke-173"),sQuery(id+"F0.wireOp",EDGE,"E6.sketch_text.stroke-174"),sQuery(id+"F0.wireOp",EDGE,"E6.sketch_text.stroke-175"),sQuery(id+"F0.wireOp",EDGE,"E6.sketch_text.stroke-176"),sQuery(id+"F0.wireOp",EDGE,"E6.sketch_text.stroke-177"),sQuery(id+"F0.wireOp",EDGE,"E6.sketch_text.stroke-178"),sQuery(id+"F0.wireOp",EDGE,"E6.sketch_text.stroke-179"),sQuery(id+"F0.wireOp",EDGE,"E6.sketch_text.stroke-180"),sQuery(id+"F0.wireOp",EDGE,"E6.sketch_text.stroke-181"),sQuery(id+"F0.wireOp",EDGE,"E6.sketch_text.stroke-182"),sQuery(id+"F0.wireOp",EDGE,"E6.sketch_text.stroke-183")])],"isStart":true})});
            var Q18;
            Q18=makeQuery(id+"F2.boolean.opBoolean","COPY",FACE,{"derivedFrom":makeQuery(id+"F2.opExtrude","CAP_FACE",FACE,{"disambiguationData":[OSD([sQuery(id+"F0.wireOp",EDGE,"E6.sketch_text.stroke-184"),sQuery(id+"F0.wireOp",EDGE,"E6.sketch_text.stroke-185"),sQuery(id+"F0.wireOp",EDGE,"E6.sketch_text.stroke-186"),sQuery(id+"F0.wireOp",EDGE,"E6.sketch_text.stroke-187"),sQuery(id+"F0.wireOp",EDGE,"E6.sketch_text.stroke-188"),sQuery(id+"F0.wireOp",EDGE,"E6.sketch_text.stroke-189"),sQuery(id+"F0.wireOp",EDGE,"E6.sketch_text.stroke-190"),sQuery(id+"F0.wireOp",EDGE,"E6.sketch_text.stroke-191"),sQuery(id+"F0.wireOp",EDGE,"E6.sketch_text.stroke-192"),sQuery(id+"F0.wireOp",EDGE,"E6.sketch_text.stroke-193"),sQuery(id+"F0.wireOp",EDGE,"E6.sketch_text.stroke-194"),sQuery(id+"F0.wireOp",EDGE,"E6.sketch_text.stroke-195"),sQuery(id+"F0.wireOp",EDGE,"E6.sketch_text.stroke-196")])],"isStart":true})});
            var Q19;
            Q19=makeQuery(id+"F2.boolean.opBoolean","COPY",FACE,{"derivedFrom":makeQuery(id+"F2.opExtrude","CAP_FACE",FACE,{"disambiguationData":[OSD([sQuery(id+"F0.wireOp",EDGE,"E6.sketch_text.stroke-197"),sQuery(id+"F0.wireOp",EDGE,"E6.sketch_text.stroke-198"),sQuery(id+"F0.wireOp",EDGE,"E6.sketch_text.stroke-199"),sQuery(id+"F0.wireOp",EDGE,"E6.sketch_text.stroke-200"),sQuery(id+"F0.wireOp",EDGE,"E6.sketch_text.stroke-201"),sQuery(id+"F0.wireOp",EDGE,"E6.sketch_text.stroke-202"),sQuery(id+"F0.wireOp",EDGE,"E6.sketch_text.stroke-203"),sQuery(id+"F0.wireOp",EDGE,"E6.sketch_text.stroke-204"),sQuery(id+"F0.wireOp",EDGE,"E6.sketch_text.stroke-205"),sQuery(id+"F0.wireOp",EDGE,"E6.sketch_text.stroke-206"),sQuery(id+"F0.wireOp",EDGE,"E6.sketch_text.stroke-207"),sQuery(id+"F0.wireOp",EDGE,"E6.sketch_text.stroke-208"),sQuery(id+"F0.wireOp",EDGE,"E6.sketch_text.stroke-209"),sQuery(id+"F0.wireOp",EDGE,"E6.sketch_text.stroke-210"),sQuery(id+"F0.wireOp",EDGE,"E6.sketch_text.stroke-211"),sQuery(id+"F0.wireOp",EDGE,"E6.sketch_text.stroke-212"),sQuery(id+"F0.wireOp",EDGE,"E6.sketch_text.stroke-213")])],"isStart":true})});
            extrude(context, id + "F3", {"entities" : qUnion([Q0, Q1, Q2, Q3, Q4, Q5, Q6, Q7, Q8, Q9, Q10, Q11, Q12, Q13, Q14, Q15, Q16, Q17, Q18, Q19]), "operationType" : NewBodyOperationType.ADD, "depth" : 25.4 * mm, "offsetDistance" : 25.4 * mm});
        }
        {
            var Q0;
            {var subQ0=sQuery(id+"F0.wireOp",EDGE,"E0.sketch_text.stroke-0");Q0=makeQuery(id+"F0.imprint","IMPRINT",FACE,{"disambiguationData":[TD([[makeQuery(id+"F0.imprint","IMPRINT",EDGE,{"derivedFrom":subQ0}),-1.0]])]});}
            var Q1;
            Q1=makeQuery(id+"F0.imprint","IMPRINT",FACE,{"disambiguationData":[TD([[makeQuery(id+"F0.imprint","IMPRINT",EDGE,{"derivedFrom":sQuery(id+"F0.wireOp",EDGE,"E0.sketch_text.stroke-6")}),-1.0]])]});
            var Q2;
            {var subQ1=sQuery(id+"F0.wireOp",EDGE,"E0.sketch_text.stroke-21");Q2=makeQuery(id+"F0.imprint","IMPRINT",FACE,{"disambiguationData":[TD([[makeQuery(id+"F0.imprint","IMPRINT",EDGE,{"derivedFrom":subQ1}),-1.0]])]});}
            var Q3;
            {var subQ0=sQuery(id+"F0.wireOp",EDGE,"E0.sketch_text.stroke-33");Q3=makeQuery(id+"F0.imprint","IMPRINT",FACE,{"disambiguationData":[TD([[makeQuery(id+"F0.imprint","IMPRINT",EDGE,{"derivedFrom":subQ0}),-1.0]])]});}
            extrude(context, id + "F4", {"entities" : qUnion([Q0, Q1, Q2, Q3]), "operationType" : NewBodyOperationType.REMOVE, "depth" : 50.8 * mm, "offsetDistance" : 25.4 * mm, "hasSecondDirection" : true, "secondDirectionOppositeDirection" : false, "secondDirectionDepth" : 38.1 * mm});
        }
        {
            var Q0;
            Q0=makeQuery(id+"F0.imprint","IMPRINT",FACE,{"disambiguationData":[TD([[makeQuery(id+"F0.imprint","IMPRINT",EDGE,{"derivedFrom":sQuery(id+"F0.wireOp",EDGE,"E0.sketch_text.stroke-6")}),-1.0]])]});
            var Q1;
            {var subQ1=sQuery(id+"F0.wireOp",EDGE,"E0.sketch_text.stroke-21");Q1=makeQuery(id+"F0.imprint","IMPRINT",FACE,{"disambiguationData":[TD([[makeQuery(id+"F0.imprint","IMPRINT",EDGE,{"derivedFrom":subQ1}),-1.0]])]});}
            var Q2;
            {var subQ0=sQuery(id+"F0.wireOp",EDGE,"E0.sketch_text.stroke-33");Q2=makeQuery(id+"F0.imprint","IMPRINT",FACE,{"disambiguationData":[TD([[makeQuery(id+"F0.imprint","IMPRINT",EDGE,{"derivedFrom":subQ0}),-1.0]])]});}
            var Q3;
            {var subQ0=sQuery(id+"F0.wireOp",EDGE,"E0.sketch_text.stroke-0");Q3=makeQuery(id+"F0.imprint","IMPRINT",FACE,{"disambiguationData":[TD([[makeQuery(id+"F0.imprint","IMPRINT",EDGE,{"derivedFrom":subQ0}),-1.0]])]});}
            extrude(context, id + "F5", {"entities" : qUnion([Q0, Q1, Q2, Q3]), "operationType" : NewBodyOperationType.REMOVE, "depth" : 12.7 * mm, "offsetDistance" : 25.4 * mm});
        }
    });
